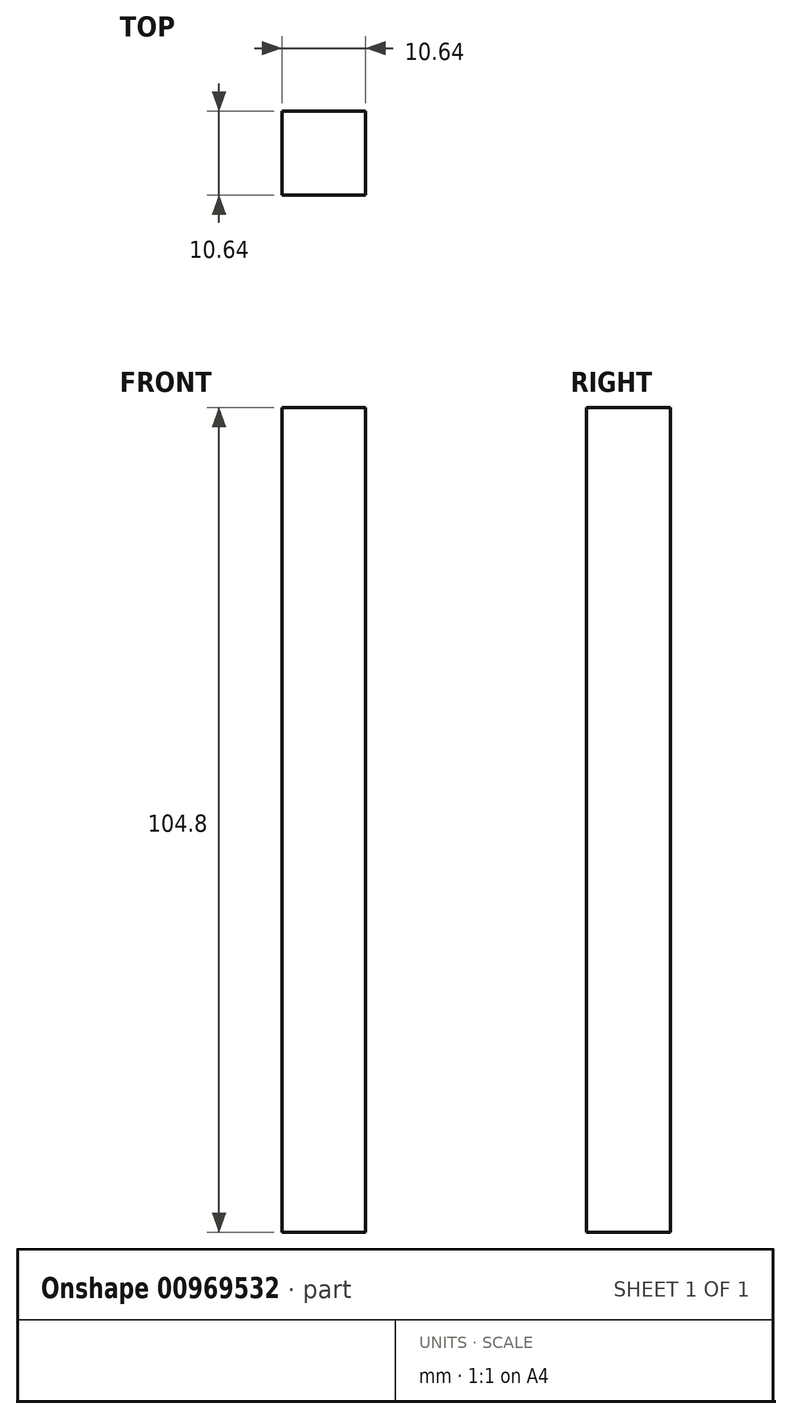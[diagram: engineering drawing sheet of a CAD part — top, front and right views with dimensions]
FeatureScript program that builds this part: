
annotation { "Feature Type Name" : "Feature", "Feature Type Description" : "" }
export const myFeature = defineFeature(function(context is Context, id is Id, definition is map)
    precondition{}
    {
        {
            var Q0;
            Q0=qCreatedBy(makeId("Front.planeOp"),FACE);
            var sketch = newSketch(context, id + "F0", { "sketchPlane" : qUnion([Q0])});
            skLineSegment(sketch, "E0.bottom", {"start": v(-10.64, 56.7) * mm, "end": v(0, 56.7) * mm});
            skLineSegment(sketch, "E0.top", {"start": v(-10.64, -48.09) * mm, "end": v(0, -48.09) * mm});
            skLineSegment(sketch, "E0.left", {"start": v(-10.64, 56.7) * mm, "end": v(-10.64, -48.09) * mm});
            skLineSegment(sketch, "E0.right", {"start": v(0, 56.7) * mm, "end": v(0, -48.09) * mm});
            skSolve(sketch);
        }
        {
            var Q0;
            Q0=makeQuery(id+"F0.imprint","IMPRINT",FACE,{"disambiguationData":[TD([[makeQuery(id+"F0.imprint","IMPRINT",EDGE,{"derivedFrom":sQuery(id+"F0.wireOp",EDGE,"E0.bottom")}),-1.0]])]});
            extrude(context, id + "F1", {"entities" : qUnion([Q0]), "depth" : 10.64 * mm, "offsetDistance" : 25.4 * mm});
        }
    });
